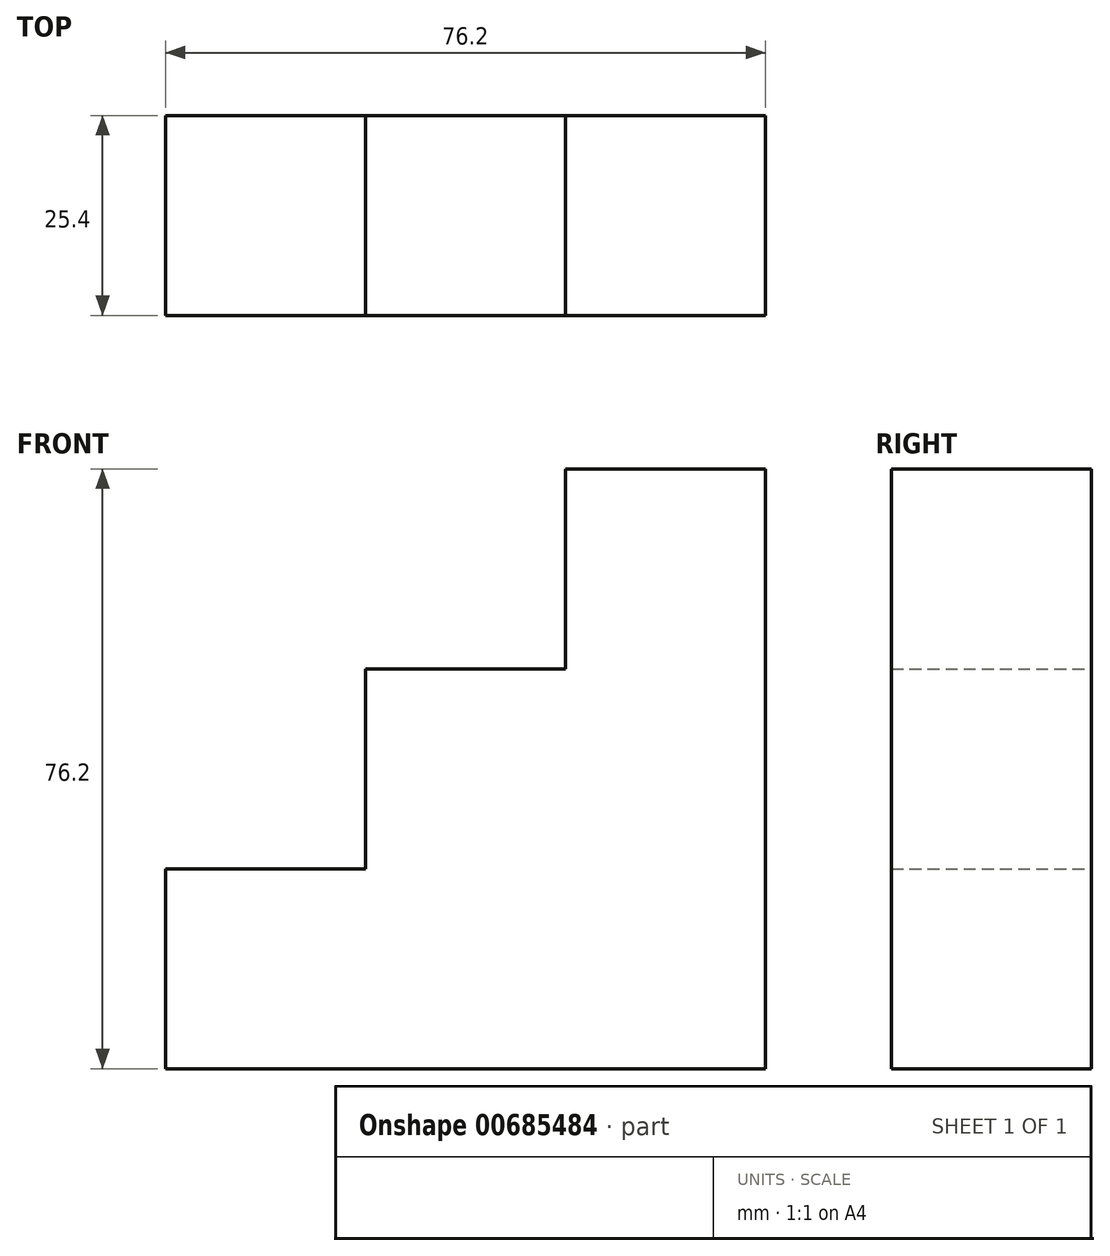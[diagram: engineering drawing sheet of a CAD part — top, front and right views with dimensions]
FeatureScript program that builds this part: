
annotation { "Feature Type Name" : "Feature", "Feature Type Description" : "" }
export const myFeature = defineFeature(function(context is Context, id is Id, definition is map)
    precondition{}
    {
        {
            var Q0;
            Q0=qCreatedBy(makeId("Front.planeOp"),FACE);
            var sketch = newSketch(context, id + "F0", { "sketchPlane" : qUnion([Q0])});
            skLineSegment(sketch, "E0", {"start": v(-62.41, 0) * mm, "end": v(13.79, 0) * mm});
            skLineSegment(sketch, "E1", {"start": v(13.79, 0) * mm, "end": v(13.79, 76.2) * mm});
            skLineSegment(sketch, "E2", {"start": v(13.79, 76.2) * mm, "end": v(-11.61, 76.2) * mm});
            skLineSegment(sketch, "E3", {"start": v(-11.61, 76.2) * mm, "end": v(-11.61, 50.8) * mm});
            skLineSegment(sketch, "E4", {"start": v(-11.61, 50.8) * mm, "end": v(-37.01, 50.8) * mm});
            skLineSegment(sketch, "E5", {"start": v(-37.01, 50.8) * mm, "end": v(-37.01, 25.4) * mm});
            skLineSegment(sketch, "E6", {"start": v(-37.01, 25.4) * mm, "end": v(-62.41, 25.4) * mm});
            skLineSegment(sketch, "E7", {"start": v(-62.41, 25.4) * mm, "end": v(-62.41, 0) * mm});
            skSolve(sketch);
        }
        {
            var Q0;
            Q0 = qSketchRegion(id + "F0", true);
            extrude(context, id + "F1", {"entities" : qUnion([Q0]), "depth" : 25.4 * mm, "offsetDistance" : 25.4 * mm});
        }
    });
